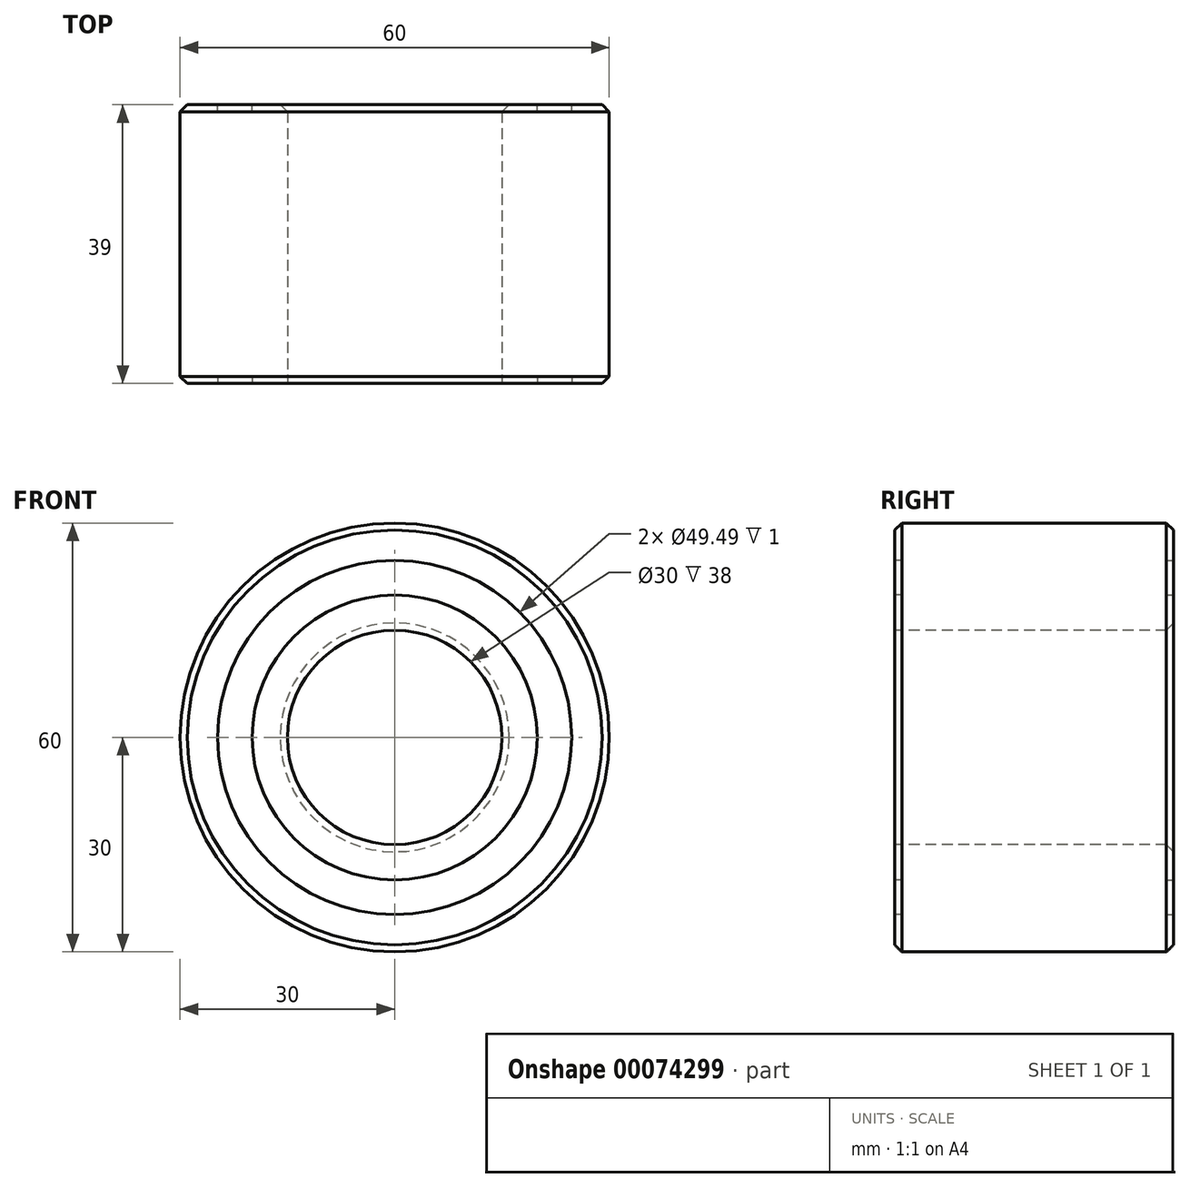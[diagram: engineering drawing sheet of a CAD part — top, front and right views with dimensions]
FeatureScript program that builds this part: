
annotation { "Feature Type Name" : "Feature", "Feature Type Description" : "" }
export const myFeature = defineFeature(function(context is Context, id is Id, definition is map)
    precondition{}
    {
        {
            var Q0;
            Q0=qCreatedBy(makeId("Front.planeOp"),FACE);
            var sketch = newSketch(context, id + "F0", { "sketchPlane" : qUnion([Q0])});
            skCircle(sketch, "E0", {"center": v(0, 0) * mm, "radius": 30 * mm});
            skSolve(sketch);
        }
        {
            var Q0;
            Q0 = qSketchRegion(id + "F0", true);
            extrude(context, id + "F1", {"entities" : qUnion([Q0]), "depth" : 39 * mm});
        }
        {
            var Q0;
            Q0=makeQuery(id+"F1.opExtrude","CAP_FACE",FACE,{"disambiguationData":[OSD([sQuery(id+"F0.wireOp",EDGE,"E0")])],"isStart":false});
            var sketch = newSketch(context, id + "F2", { "sketchPlane" : qUnion([Q0])});
            skCircle(sketch, "E1", {"center": v(0, 0) * mm, "radius": 15 * mm});
            skSolve(sketch);
        }
        {
            var Q0;
            Q0=makeQuery(id+"F2.imprint","IMPRINT",FACE,{"disambiguationData":[TD([[makeQuery(id+"F2.imprint","IMPRINT",EDGE,{"derivedFrom":sQuery(id+"F2.wireOp",EDGE,"E1")}),1.0]])]});
            extrude(context, id + "F3", {"entities" : qUnion([Q0]), "operationType" : NewBodyOperationType.REMOVE, "endBound" : BoundingType.THROUGH_ALL, "oppositeDirection" : true, "depth" : 25 * mm});
        }
        {
            var Q0;
            Q0=makeQuery(id+"F1.opExtrude","CAP_EDGE",EDGE,{"disambiguationData":[OSD([sQuery(id+"F0.wireOp",EDGE,"E0")])],"isStart":false});
            var Q1;
            Q1=makeQuery(id+"F3.boolean.opBoolean","COPY",EDGE,{"derivedFrom":makeQuery(id+"F3.opExtrude","CAP_EDGE",EDGE,{"disambiguationData":[OSD([sQuery(id+"F2.wireOp",EDGE,"E1")])],"isStart":true})});
            var Q2;
            Q2=makeQuery(id+"F1.opExtrude","CAP_EDGE",EDGE,{"disambiguationData":[OSD([sQuery(id+"F0.wireOp",EDGE,"E0")])],"isStart":true});
            var Q3;
            Q3=makeQuery(id+"F3.boolean.opBoolean","INTERSECT",EDGE,{"derivedFrom":[makeQuery(id+"F1.opExtrude","CAP_FACE",FACE,{"disambiguationData":[OSD([sQuery(id+"F0.wireOp",EDGE,"E0")])],"isStart":true}),makeQuery(id+"F3.opExtrude","SWEPT_FACE",FACE,{"disambiguationData":[OSD([sQuery(id+"F2.wireOp",EDGE,"E1")])]})]});
            chamfer(context, id + "F4", {"entities" : qUnion([Q0, Q1, Q2, Q3]), "width" : 1 * mm, "tangentPropagation" : true});
        }
        {
            var Q0;
            Q0=makeQuery(id+"F1.opExtrude","CAP_FACE",FACE,{"disambiguationData":[OSD([sQuery(id+"F0.wireOp",EDGE,"E0")])],"isStart":true});
            var sketch = newSketch(context, id + "F5", { "sketchPlane" : qUnion([Q0])});
            skCircle(sketch, "E2", {"center": v(0, 0) * mm, "radius": 19.92 * mm});
            skCircle(sketch, "E3", {"center": v(0, 0) * mm, "radius": 24.74 * mm});
            skSolve(sketch);
        }
        {
            var Q0;
            Q0 = qSketchRegion(id + "F5", true);
            extrude(context, id + "F6", {"entities" : qUnion([Q0]), "operationType" : NewBodyOperationType.REMOVE, "oppositeDirection" : true, "depth" : 1 * mm});
        }
        {
            var Q0;
            Q0=makeQuery(id+"F1.opExtrude","CAP_FACE",FACE,{"disambiguationData":[OSD([sQuery(id+"F0.wireOp",EDGE,"E0")])],"isStart":false});
            var sketch = newSketch(context, id + "F7", { "sketchPlane" : qUnion([Q0])});
            skCircle(sketch, "E4.0", {"center": v(0, 0) * mm, "radius": 19.92 * mm});
            skCircle(sketch, "E4.1", {"center": v(0, 0) * mm, "radius": 24.74 * mm});
            skSolve(sketch);
        }
        {
            var Q0;
            Q0=makeQuery(id+"F7.imprint","IMPRINT",FACE,{"disambiguationData":[TD([[makeQuery(id+"F7.imprint","IMPRINT",EDGE,{"derivedFrom":sQuery(id+"F7.wireOp",EDGE,"E4.0")}),-1.0]])]});
            extrude(context, id + "F8", {"entities" : qUnion([Q0]), "operationType" : NewBodyOperationType.REMOVE, "oppositeDirection" : true, "depth" : 1 * mm});
        }
    });
